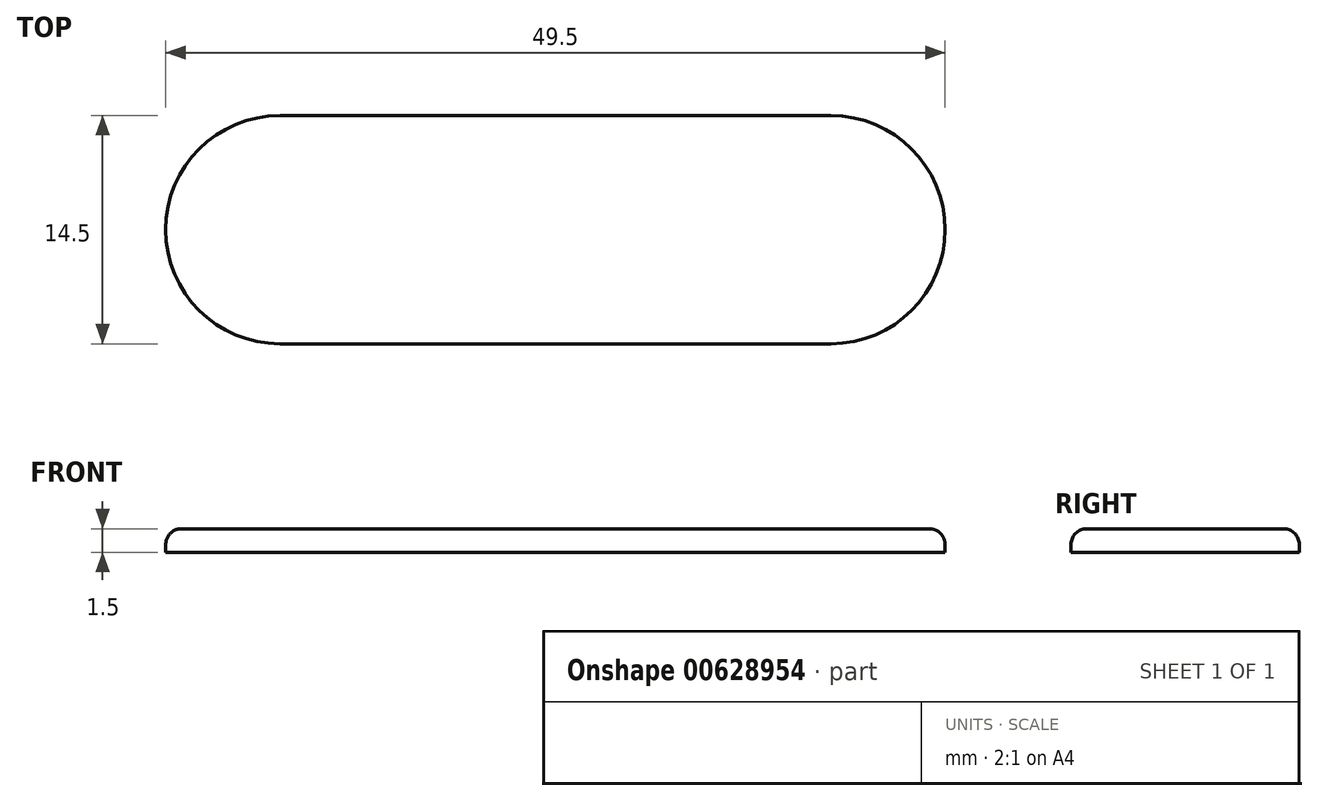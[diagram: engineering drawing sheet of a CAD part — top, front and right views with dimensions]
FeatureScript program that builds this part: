
annotation { "Feature Type Name" : "Feature", "Feature Type Description" : "" }
export const myFeature = defineFeature(function(context is Context, id is Id, definition is map)
    precondition{}
    {
        {
            var Q0;
            Q0=qCreatedBy(makeId("Top.planeOp"),FACE);
            var sketch = newSketch(context, id + "F0", { "sketchPlane" : qUnion([Q0])});
            skLineSegment(sketch, "E0.bottom", {"start": v(-25.03, 3.67) * mm, "end": v(9.97, 3.67) * mm});
            skLineSegment(sketch, "E0.top", {"start": v(-25.03, -10.83) * mm, "end": v(9.97, -10.83) * mm});
            skLineSegment(sketch, "E0.left", {"start": v(-25.03, 3.67) * mm, "end": v(-25.03, -10.83) * mm});
            skLineSegment(sketch, "E0.right", {"start": v(9.97, 3.67) * mm, "end": v(9.97, -10.83) * mm});
            skArc(sketch, "E1", {"start": v(-25.03, 3.67) * mm, "mid": v(-32.28, -3.58) * mm, "end": v(-25.03, -10.83) * mm});
            skArc(sketch, "E2", {"start": v(9.97, -10.83) * mm, "mid": v(17.22, -3.58) * mm, "end": v(9.97, 3.67) * mm});
            skSolve(sketch);
        }
        {
            var Q0;
            Q0 = qSketchRegion(id + "F0", true);
            extrude(context, id + "F1", {"entities" : qUnion([Q0]), "depth" : 1.5 * mm, "offsetDistance" : 25 * mm});
        }
        {
            var Q0;
            Q0=makeQuery(id+"F1.opExtrude","CAP_FACE",FACE,{"disambiguationData":[OSD([sQuery(id+"F0.wireOp",EDGE,"E0.bottom"),sQuery(id+"F0.wireOp",EDGE,"E0.top"),sQuery(id+"F0.wireOp",EDGE,"E1"),sQuery(id+"F0.wireOp",EDGE,"E2")])],"isStart":false});
            fillet(context, id + "F2", {"entities" : qUnion([Q0]), "radius" : 1 * mm, "tangentPropagation" : true, "allowEdgeOverflow" : false});
        }
    });
